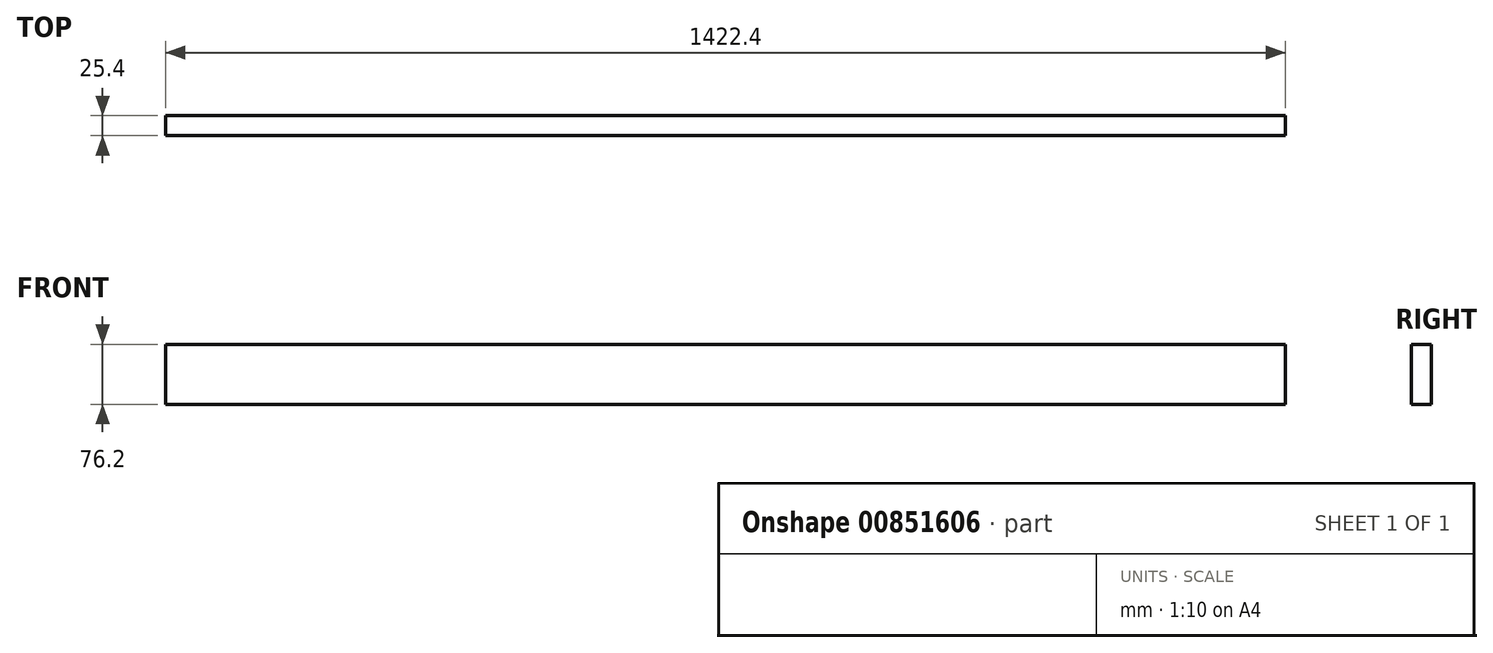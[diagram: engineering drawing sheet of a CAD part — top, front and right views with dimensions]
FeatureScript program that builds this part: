
annotation { "Feature Type Name" : "Feature", "Feature Type Description" : "" }
export const myFeature = defineFeature(function(context is Context, id is Id, definition is map)
    precondition{}
    {
        {
            var Q0;
            Q0=qCreatedBy(makeId("Front.planeOp"),FACE);
            var sketch = newSketch(context, id + "F0", { "sketchPlane" : qUnion([Q0])});
            skLineSegment(sketch, "E0", {"start": v(-803.07, 43.36) * mm, "end": v(619.33, 43.36) * mm});
            skLineSegment(sketch, "E1", {"start": v(-803.07, 43.36) * mm, "end": v(-803.07, -32.84) * mm});
            skLineSegment(sketch, "E2", {"start": v(619.33, 43.36) * mm, "end": v(619.33, -32.84) * mm});
            skLineSegment(sketch, "E3", {"start": v(619.33, -32.84) * mm, "end": v(-803.07, -32.84) * mm});
            skSolve(sketch);
        }
        {
            var Q0;
            Q0 = qSketchRegion(id + "F0", true);
            extrude(context, id + "F1", {"entities" : qUnion([Q0]), "depth" : 25.4 * mm, "offsetDistance" : 25.4 * mm});
        }
    });
